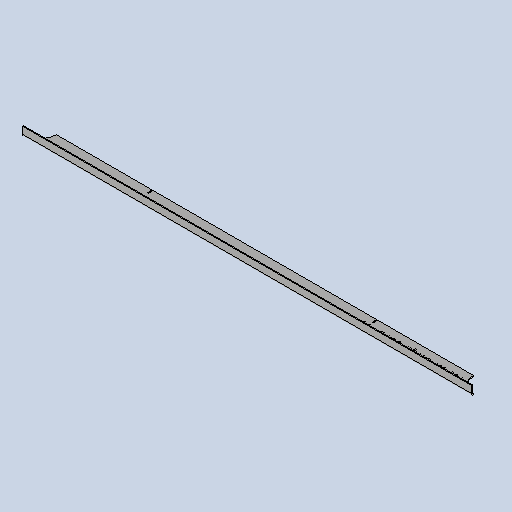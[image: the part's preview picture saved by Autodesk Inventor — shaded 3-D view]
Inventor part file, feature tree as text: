
AUTODESK INVENTOR PART (.ipt)
format: ipt  version: 2025 (Build 290162010, 162A)  size: 321,024 bytes
history: native  units: mm
features: other x5, sheet_metal_op x4, sketch x4, extrude x1
ambient origin geometry x8: Origin, YZ Plane, XZ Plane, XY Plane, X Axis, Y Axis, Z Axis, Center Point
bodies: Solid1 (feature_tree)
feature tree (14):
  sheet_metal_op  "Face1"
  sheet_metal_op  "Flange1"
  extrude  "Extrusion1"  Depth=39.0mm
  other  "Mark2"
  other  "A-Side Definition"
  sketch  "Sketch1"  dims[d0=980.0mm d1=39.0mm]
  other  "Plate1"
  sketch  "Sketch2"  dims[d2=2.0mm]
  other  "Plate2"
  sheet_metal_op  "Bend1"
  sheet_metal_op  "Corner1"
  sketch  "Sketch5"  dims[d3=2.0mm]
  sketch  "Sketch9"  dims[d4=1.0mm d5=4.0mm d6=2.75mm d7=20.0mm d8=90.0deg d9=2.75mm d10=8.0mm d11=2.0mm d12=2.75mm d15=0.0mm d16=0.0mm d40=200.0mm d41=12.0mm d45=70.0mm d48=2.1mm d49=490.0mm d51=29.0mm d52=10.0mm]
  other  "Definition1"
